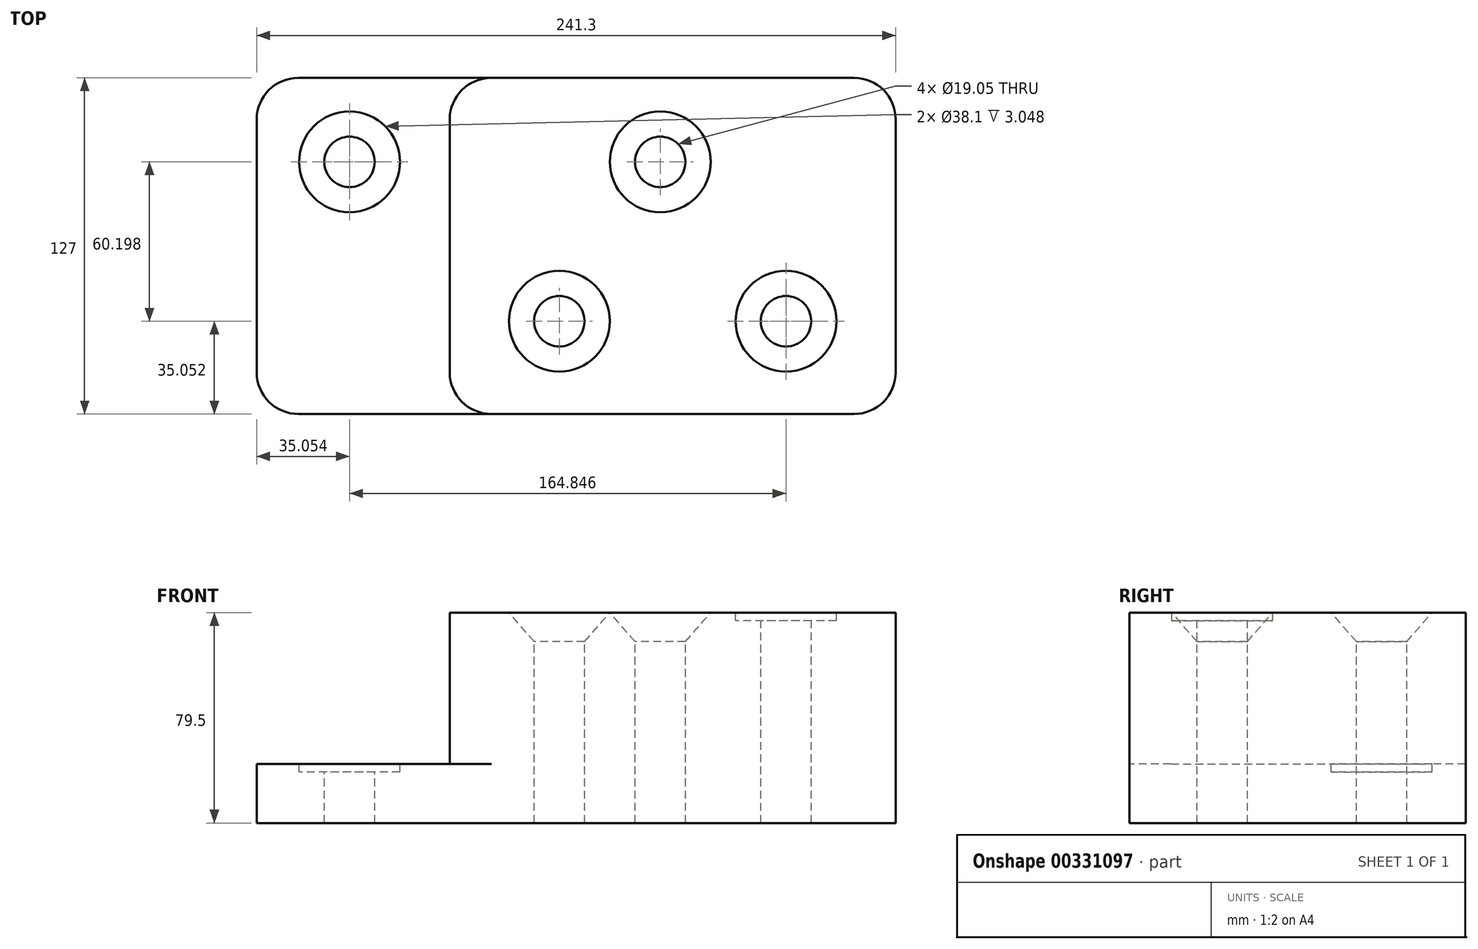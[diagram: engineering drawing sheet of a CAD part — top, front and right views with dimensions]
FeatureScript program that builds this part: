
annotation { "Feature Type Name" : "Feature", "Feature Type Description" : "" }
export const myFeature = defineFeature(function(context is Context, id is Id, definition is map)
    precondition{}
    {
        {
            var Q0;
            Q0=qCreatedBy(makeId("Top.planeOp"),FACE);
            var sketch = newSketch(context, id + "F0", { "sketchPlane" : qUnion([Q0])});
            skLineSegment(sketch, "E0.bottom", {"start": v(0, 0) * mm, "end": v(168.4, 0) * mm});
            skLineSegment(sketch, "E0.top", {"start": v(0, 127) * mm, "end": v(168.4, 127) * mm});
            skLineSegment(sketch, "E0.left", {"start": v(0, 0) * mm, "end": v(0, 127) * mm});
            skLineSegment(sketch, "E0.right", {"start": v(168.4, 0) * mm, "end": v(168.4, 127) * mm});
            skLineSegment(sketch, "E1.bottom", {"start": v(168.4, 0) * mm, "end": v(-72.9, 0) * mm});
            skLineSegment(sketch, "E1.top", {"start": v(168.4, 127) * mm, "end": v(-72.9, 127) * mm});
            skLineSegment(sketch, "E1.right", {"start": v(-72.9, 0) * mm, "end": v(-72.9, 127) * mm});
            skSolve(sketch);
        }
        {
            var Q0;
            {var subQ0=sQuery(id+"F0.wireOp",EDGE,"E0.left");Q0=makeQuery(id+"F0.imprint","IMPRINT",FACE,{"disambiguationData":[TD([[makeQuery(id+"F0.imprint","IMPRINT",EDGE,{"derivedFrom":subQ0}),-1.0]])]});}
            extrude(context, id + "F1", {"entities" : qUnion([Q0]), "depth" : 79.5 * mm});
        }
        {
            var Q0;
            Q0 = qSketchRegion(id + "F0", true);
            extrude(context, id + "F2", {"entities" : qUnion([Q0]), "operationType" : NewBodyOperationType.ADD, "depth" : 22.35 * mm});
        }
        {
            var Q0;
            Q0=makeQuery(id+"F1.opExtrude","SWEPT_EDGE",EDGE,{"disambiguationData":[OSD([sQuery(id+"F0.wireOp",EDGE,"E1.bottom"),sQuery(id+"F0.wireOp",EDGE,"E0.right")])]});
            var Q1;
            Q1=makeQuery(id+"F1.opExtrude","SWEPT_EDGE",EDGE,{"disambiguationData":[OSD([sQuery(id+"F0.wireOp",EDGE,"E1.top"),sQuery(id+"F0.wireOp",EDGE,"E0.right")])]});
            var Q2;
            Q2=makeQuery(id+"F1.opExtrude","SWEPT_EDGE",EDGE,{"disambiguationData":[OSD([sQuery(id+"F0.wireOp",EDGE,"E0.left"),sQuery(id+"F0.wireOp",EDGE,"E1.bottom")])]});
            var Q3;
            Q3=makeQuery(id+"F1.opExtrude","SWEPT_EDGE",EDGE,{"disambiguationData":[OSD([sQuery(id+"F0.wireOp",EDGE,"E0.left"),sQuery(id+"F0.wireOp",EDGE,"E1.top")])]});
            fillet(context, id + "F3", {"entities" : qUnion([Q0, Q1, Q2, Q3]), "radius" : 15.75 * mm, "tangentPropagation" : true, "allowEdgeOverflow" : false});
        }
        {
            var Q0;
            Q0=makeQuery(id+"F2.opExtrude","SWEPT_EDGE",EDGE,{"disambiguationData":[OSD([sQuery(id+"F0.wireOp",EDGE,"E1.top"),sQuery(id+"F0.wireOp",EDGE,"E1.right")])]});
            var Q1;
            Q1=makeQuery(id+"F2.opExtrude","SWEPT_EDGE",EDGE,{"disambiguationData":[OSD([sQuery(id+"F0.wireOp",EDGE,"E1.bottom"),sQuery(id+"F0.wireOp",EDGE,"E1.right")])]});
            fillet(context, id + "F4", {"entities" : qUnion([Q0, Q1]), "radius" : 15.75 * mm, "tangentPropagation" : true, "allowEdgeOverflow" : false});
        }
        {
            var Q0;
            Q0=makeQuery(id+"F1.opExtrude","CAP_FACE",FACE,{"disambiguationData":[OSD([sQuery(id+"F0.wireOp",EDGE,"E0.left"),sQuery(id+"F0.wireOp",EDGE,"E1.bottom"),sQuery(id+"F0.wireOp",EDGE,"E1.top"),sQuery(id+"F0.wireOp",EDGE,"E0.right")])],"isStart":false});
            var sketch = newSketch(context, id + "F5", { "sketchPlane" : qUnion([Q0])});
            skPoint(sketch, "E2", {"position": v(79.5, 95.25) * mm});
            skPoint(sketch, "E3", {"position": v(41.4, 35.05) * mm});
            skPoint(sketch, "E4", {"position": v(127, 35.05) * mm});
            skSolve(sketch);
        }
        {
            var Q0;
            Q0=makeQuery(id+"F2.opExtrude","CAP_FACE",FACE,{"disambiguationData":[OSD([sQuery(id+"F0.wireOp",EDGE,"E1.bottom"),sQuery(id+"F0.wireOp",EDGE,"E1.top"),sQuery(id+"F0.wireOp",EDGE,"E0.right"),sQuery(id+"F0.wireOp",EDGE,"E1.right")])],"isStart":false});
            var sketch = newSketch(context, id + "F6", { "sketchPlane" : qUnion([Q0])});
            skPoint(sketch, "E5", {"position": v(-37.85, 95.25) * mm});
            skSolve(sketch);
        }
        {
            var Q0;
            Q0=sQuery(id+"F5.wireOp",VERTEX,"E2");
            var Q1;
            Q1=sQuery(id+"F5.wireOp",VERTEX,"E3");
            var Q2;
            Q2=makeQuery(id+"F1.opExtrude","SWEPT_BODY",BODY,{"disambiguationData":[OSD([sQuery(id+"F0.wireOp",EDGE,"E0.left"),sQuery(id+"F0.wireOp",EDGE,"E1.bottom"),sQuery(id+"F0.wireOp",EDGE,"E1.top"),sQuery(id+"F0.wireOp",EDGE,"E0.right")])]});
            hole(context, id + "F7", {"style" : HoleStyle.C_SINK, "endStyle" : HoleEndStyle.THROUGH, "holeDiameter" : 19.05 * mm, "cSinkDiameter" : 38.1 * mm, "cSinkAngle" : 82 * degree, "tappedDepth" : 12.7 * mm, "tapClearance" : 3, "locations" : qUnion([Q0, Q1]), "scope" : qUnion([Q2])});
        }
        {
            var Q0;
            Q0=sQuery(id+"F5.wireOp",VERTEX,"E4");
            var Q1;
            Q1=sQuery(id+"F6.wireOp",VERTEX,"E5");
            var Q2;
            Q2=makeQuery(id+"F1.opExtrude","SWEPT_BODY",BODY,{"disambiguationData":[OSD([sQuery(id+"F0.wireOp",EDGE,"E0.left"),sQuery(id+"F0.wireOp",EDGE,"E1.bottom"),sQuery(id+"F0.wireOp",EDGE,"E1.top"),sQuery(id+"F0.wireOp",EDGE,"E0.right")])]});
            hole(context, id + "F8", {"style" : HoleStyle.C_BORE, "endStyle" : HoleEndStyle.THROUGH, "holeDiameter" : 19.05 * mm, "cBoreDiameter" : 38.1 * mm, "cBoreDepth" : 3.05 * mm, "tappedDepth" : 12.7 * mm, "tapClearance" : 3, "locations" : qUnion([Q0, Q1]), "scope" : qUnion([Q2])});
        }
    });
